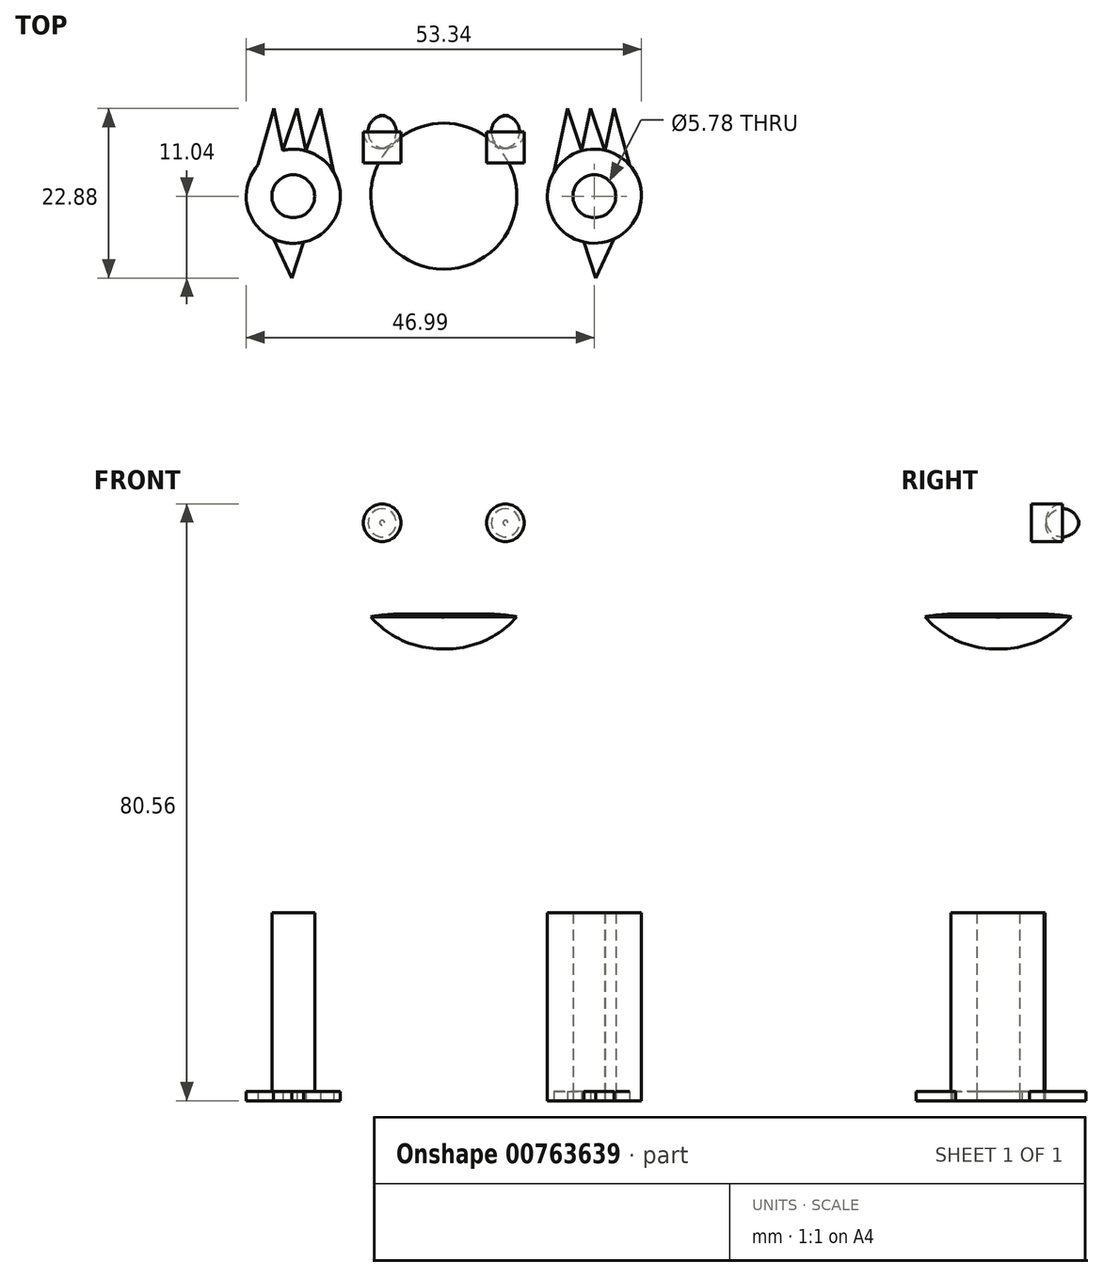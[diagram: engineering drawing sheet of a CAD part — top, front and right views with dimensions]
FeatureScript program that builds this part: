
annotation { "Feature Type Name" : "Feature", "Feature Type Description" : "" }
export const myFeature = defineFeature(function(context is Context, id is Id, definition is map)
    precondition{}
    {
        {
            var Q0;
            Q0=qCreatedBy(makeId("Top.planeOp"),FACE);
            var sketch = newSketch(context, id + "F0", { "sketchPlane" : qUnion([Q0])});
            skCircle(sketch, "E0", {"center": v(-20.32, 0) * mm, "radius": 6.35 * mm});
            skLineSegment(sketch, "E1", {"start": v(-23, -5.75) * mm, "end": v(-20.49, -11.04) * mm});
            skLineSegment(sketch, "E2", {"start": v(-18.95, -6.2) * mm, "end": v(-20.49, -11.04) * mm});
            skLineSegment(sketch, "E3.MirrorCS", {"start": v(18.95, -6.2) * mm, "end": v(20.49, -11.04) * mm});
            skLineSegment(sketch, "E4.MirrorCS", {"start": v(23, -5.75) * mm, "end": v(20.49, -11.04) * mm});
            skCircle(sketch, "E5.MirrorC", {"center": v(20.32, 0) * mm, "radius": 2.9 * mm});
            skCircle(sketch, "E6.MirrorC", {"center": v(20.32, 0) * mm, "radius": 6.35 * mm});
            skLineSegment(sketch, "E7", {"start": v(14.86, 3.24) * mm, "end": v(16.67, 11.84) * mm});
            skLineSegment(sketch, "E8", {"start": v(16.67, 11.84) * mm, "end": v(18.6, 6.12) * mm});
            skLineSegment(sketch, "E9", {"start": v(18.6, 6.12) * mm, "end": v(19.81, 11.84) * mm});
            skLineSegment(sketch, "E10", {"start": v(19.81, 11.84) * mm, "end": v(21.75, 6.12) * mm});
            skLineSegment(sketch, "E11", {"start": v(21.75, 6.12) * mm, "end": v(22.96, 11.84) * mm});
            skLineSegment(sketch, "E12", {"start": v(22.96, 11.84) * mm, "end": v(25.07, 4.22) * mm});
            skLineSegment(sketch, "E13.MirrorCS", {"start": v(-18.6, 6.12) * mm, "end": v(-19.81, 11.84) * mm});
            skCircle(sketch, "E14.MirrorC", {"center": v(-20.32, 0) * mm, "radius": 2.9 * mm});
            skLineSegment(sketch, "E15.MirrorCS", {"start": v(-16.67, 11.84) * mm, "end": v(-18.6, 6.12) * mm});
            skLineSegment(sketch, "E16.MirrorCS", {"start": v(-14.86, 3.24) * mm, "end": v(-16.67, 11.84) * mm});
            skLineSegment(sketch, "E17.MirrorCS", {"start": v(-22.96, 11.84) * mm, "end": v(-25.07, 4.22) * mm});
            skLineSegment(sketch, "E18.MirrorCS", {"start": v(-19.81, 11.84) * mm, "end": v(-21.75, 6.12) * mm});
            skLineSegment(sketch, "E19.MirrorCS", {"start": v(-21.75, 6.12) * mm, "end": v(-22.96, 11.84) * mm});
            skSolve(sketch);
        }
        {
            var Q0;
            Q0=makeQuery(id+"F0.imprint","IMPRINT",FACE,{"disambiguationData":[TD([[makeQuery(id+"F0.imprint","IMPRINT",EDGE,{"derivedFrom":sQuery(id+"F0.wireOp",EDGE,"E14.MirrorC")}),1.0]])]});
            var Q1;
            Q1=makeQuery(id+"F0.imprint","IMPRINT",FACE,{"disambiguationData":[TD([[makeQuery(id+"F0.imprint","IMPRINT",EDGE,{"derivedFrom":sQuery(id+"F0.wireOp",EDGE,"E5.MirrorC")}),-1.0]])]});
            extrude(context, id + "F1", {"entities" : qUnion([Q0, Q1]), "depth" : 25.4 * mm, "offsetDistance" : 25.4 * mm});
        }
        {
            var Q0;
            Q0=qCreatedBy(makeId("Front.planeOp"),FACE);
            var sketch = newSketch(context, id + "F2", { "sketchPlane" : qUnion([Q0])});
            skArc(sketch, "E20", {"start": v(0, 65.16) * mm, "mid": v(-32.14, 38.92) * mm, "end": v(0, 12.69) * mm});
            skLineSegment(sketch, "E21", {"start": v(0, 65.16) * mm, "end": v(0, 12.69) * mm});
            skSolve(sketch);
        }
        {
            var Q0;
            Q0=makeQuery(id+"F2.imprint","IMPRINT",FACE,{"disambiguationData":[TD([[makeQuery(id+"F2.imprint","IMPRINT",EDGE,{"derivedFrom":sQuery(id+"F2.wireOp",EDGE,"E20")}),1.0]])]});
            var Q1;
            Q1=sQuery(id+"F2.wireOp",EDGE,"E21");
            revolve(context, id + "F3", {"surfaceOperationType" : NewSurfaceOperationType.NEW, "entities" : qUnion([Q0]), "axis" : qUnion([Q1]), "revolveType" : RevolveType.FULL});
        }
        {
            var Q0;
            Q0=makeQuery(id+"F0.imprint","IMPRINT",FACE,{"disambiguationData":[TD([[makeQuery(id+"F0.imprint","IMPRINT",EDGE,{"derivedFrom":sQuery(id+"F0.wireOp",EDGE,"E14.MirrorC")}),-1.0]])]});
            extrude(context, id + "F4", {"entities" : qUnion([Q0]), "operationType" : NewBodyOperationType.ADD, "depth" : 1.27 * mm, "offsetDistance" : 25.4 * mm});
        }
        {
            var Q0;
            {var subQ0=sQuery(id+"F0.wireOp",EDGE,"E17.MirrorCS");Q0=makeQuery(id+"F0.imprint","IMPRINT",FACE,{"disambiguationData":[TD([[makeQuery(id+"F0.imprint","IMPRINT",EDGE,{"derivedFrom":subQ0}),1.0]])]});}
            extrude(context, id + "F5", {"entities" : qUnion([Q0]), "operationType" : NewBodyOperationType.ADD, "depth" : 1.27 * mm, "offsetDistance" : 25.4 * mm});
        }
        {
            var Q0;
            {var subQ0=sQuery(id+"F0.wireOp",EDGE,"E13.MirrorCS");Q0=makeQuery(id+"F0.imprint","IMPRINT",FACE,{"disambiguationData":[TD([[makeQuery(id+"F0.imprint","IMPRINT",EDGE,{"derivedFrom":subQ0}),1.0]])]});}
            var Q1;
            {var subQ0=sQuery(id+"F0.wireOp",EDGE,"E15.MirrorCS");Q1=makeQuery(id+"F0.imprint","IMPRINT",FACE,{"disambiguationData":[TD([[makeQuery(id+"F0.imprint","IMPRINT",EDGE,{"derivedFrom":subQ0}),1.0]])]});}
            var Q2;
            {var subQ0=sQuery(id+"F0.wireOp",EDGE,"E2");Q2=makeQuery(id+"F0.imprint","IMPRINT",FACE,{"disambiguationData":[TD([[makeQuery(id+"F0.imprint","IMPRINT",EDGE,{"derivedFrom":subQ0}),-1.0]])]});}
            var Q3;
            {var subQ0=sQuery(id+"F0.wireOp",EDGE,"E3.MirrorCS");Q3=makeQuery(id+"F0.imprint","IMPRINT",FACE,{"disambiguationData":[TD([[makeQuery(id+"F0.imprint","IMPRINT",EDGE,{"derivedFrom":subQ0}),1.0]])]});}
            var Q4;
            {var subQ0=sQuery(id+"F0.wireOp",EDGE,"E7");Q4=makeQuery(id+"F0.imprint","IMPRINT",FACE,{"disambiguationData":[TD([[makeQuery(id+"F0.imprint","IMPRINT",EDGE,{"derivedFrom":subQ0}),-1.0]])]});}
            var Q5;
            {var subQ0=sQuery(id+"F0.wireOp",EDGE,"E9");Q5=makeQuery(id+"F0.imprint","IMPRINT",FACE,{"disambiguationData":[TD([[makeQuery(id+"F0.imprint","IMPRINT",EDGE,{"derivedFrom":subQ0}),-1.0]])]});}
            var Q6;
            Q6=makeQuery(id+"F0.imprint","IMPRINT",FACE,{"disambiguationData":[TD([[makeQuery(id+"F0.imprint","IMPRINT",EDGE,{"derivedFrom":sQuery(id+"F0.wireOp",EDGE,"E5.MirrorC")}),1.0]])]});
            var Q7;
            {var subQ0=sQuery(id+"F0.wireOp",EDGE,"E12");Q7=makeQuery(id+"F0.imprint","IMPRINT",FACE,{"disambiguationData":[TD([[makeQuery(id+"F0.imprint","IMPRINT",EDGE,{"derivedFrom":subQ0}),-1.0]])]});}
            extrude(context, id + "F6", {"entities" : qUnion([Q0, Q1, Q2, Q3, Q4, Q5, Q6, Q7]), "depth" : 1.27 * mm, "offsetDistance" : 25.4 * mm});
        }
        {
            var Q0;
            Q0=qCreatedBy(makeId("Front.planeOp"),FACE);
            var sketch = newSketch(context, id + "F7", { "sketchPlane" : qUnion([Q0])});
            skLineSegment(sketch, "E22", {"start": v(0, 61) * mm, "end": v(0, 86.4) * mm});
            skArc(sketch, "E23", {"start": v(0, 86.4) * mm, "mid": v(-13, 73.7) * mm, "end": v(0, 61) * mm});
            skSolve(sketch);
        }
        {
            var Q0;
            Q0=makeQuery(id+"F7.imprint","IMPRINT",FACE,{"disambiguationData":[TD([[makeQuery(id+"F7.imprint","IMPRINT",EDGE,{"derivedFrom":sQuery(id+"F7.wireOp",EDGE,"E22")}),1.0]])]});
            var Q1;
            Q1=sQuery(id+"F7.wireOp",EDGE,"E22");
            revolve(context, id + "F8", {"operationType" : NewBodyOperationType.ADD, "surfaceOperationType" : NewSurfaceOperationType.NEW, "entities" : qUnion([Q0]), "axis" : qUnion([Q1]), "revolveType" : RevolveType.FULL});
        }
        {
            var Q0;
            Q0=qCreatedBy(makeId("Front.planeOp"),FACE);
            var sketch = newSketch(context, id + "F9", { "sketchPlane" : qUnion([Q0])});
            skCircle(sketch, "E24", {"center": v(0, 75.92) * mm, "radius": 1.47 * mm});
            skSolve(sketch);
        }
        {
            var Q0;
            Q0=sQuery(id+"F9.wireOp",EDGE,"E24");
            extrude(context, id + "F10", {"bodyType" : ToolBodyType.SURFACE, "surfaceEntities" : qUnion([Q0]), "oppositeDirection" : true, "depth" : 13.46 * mm, "offsetDistance" : 25.4 * mm});
        }
        {
            var Q0;
            Q0=qCreatedBy(makeId("Right.planeOp"),FACE);
            var sketch = newSketch(context, id + "F11", { "sketchPlane" : qUnion([Q0])});
            skPoint(sketch, "E25", {"position": v(17.1, 75.94) * mm});
            skSolve(sketch);
        }
        {
            var Q0;
            Q0=makeQuery(id+"F10.opExtrude","SWEPT_BODY",BODY,{"disambiguationData":[OSD([sQuery(id+"F9.wireOp",EDGE,"E24")])]});
            var Q1;
            Q1=makeQuery(id+"F10.opExtrude","CAP_EDGE",EDGE,{"disambiguationData":[OSD([sQuery(id+"F9.wireOp",EDGE,"E24")])],"isStart":false});
            var Q2;
            Q2=sQuery(id+"F11.wireOp",VERTEX,"E25");
            loft(context, id + "F12", {"bodyType" : ToolBodyType.SURFACE, "surfaceOperationType" : NewSurfaceOperationType.ADD, "sheetProfilesArray" : [{ "sheetProfileEntities" : qUnion([Q0]) }], "wireProfilesArray" : [{ "wireProfileEntities" : qUnion([Q1]) }, { "wireProfileEntities" : qUnion([Q2]) }]});
        }
        {
            var Q0;
            Q0=qCreatedBy(makeId("Front.planeOp"),FACE);
            cPlane(context, id + "F13", {"entities" : qUnion([Q0]), "cplaneType" : CPlaneType.OFFSET, "offset" : 10.16 * mm, "oppositeDirection" : true, "width" : 152.4 * mm, "height" : 152.4 * mm});
        }
        {
            var Q0;
            Q0=qCreatedBy(id+"F13.planeOp",FACE);
            var sketch = newSketch(context, id + "F14", { "sketchPlane" : qUnion([Q0])});
            skCircle(sketch, "E26", {"center": v(8.32, 78.02) * mm, "radius": 2.54 * mm});
            skCircle(sketch, "E27", {"center": v(-8.32, 78.02) * mm, "radius": 2.54 * mm});
            skSolve(sketch);
        }
        {
            var Q0;
            Q0 = qSketchRegion(id + "F14", true);
            extrude(context, id + "F15", {"entities" : qUnion([Q0]), "oppositeDirection" : true, "depth" : 0.76 * mm, "offsetDistance" : 25.4 * mm, "hasSecondDirection" : true, "secondDirectionOppositeDirection" : false, "secondDirectionDepth" : 5.66 * mm});
        }
        {
            var Q0;
            Q0=makeQuery(id+"F15.opExtrude","CAP_FACE",FACE,{"disambiguationData":[OSD([sQuery(id+"F14.wireOp",EDGE,"E27")])],"isStart":false});
            var Q1;
            Q1=makeQuery(id+"F15.opExtrude","CAP_FACE",FACE,{"disambiguationData":[OSD([sQuery(id+"F14.wireOp",EDGE,"E26")])],"isStart":false});
            fillet(context, id + "F16", {"entities" : qUnion([Q0, Q1]), "radius" : 2.22 * mm, "tangentPropagation" : true, "allowEdgeOverflow" : false});
        }
        {
            var Q0;
            Q0=qCreatedBy(makeId("Right.planeOp"),FACE);
            cPlane(context, id + "F17", {"entities" : qUnion([Q0]), "cplaneType" : CPlaneType.OFFSET, "offset" : 30.48 * mm, "width" : 152.4 * mm, "height" : 152.4 * mm});
        }
        {
            var Q0;
            Q0=qCreatedBy(id+"F17.planeOp",FACE);
            var sketch = newSketch(context, id + "F18", { "sketchPlane" : qUnion([Q0])});
            skLineSegment(sketch, "E28", {"start": v(-10.4, 41.11) * mm, "end": v(11.18, 41.11) * mm});
            skArc(sketch, "E29", {"start": v(-10.4, 41.11) * mm, "mid": v(0.39, 30.32) * mm, "end": v(11.18, 41.11) * mm});
            skSolve(sketch);
        }
        {
            var Q0;
            Q0=sQuery(id+"F18.wireOp",EDGE,"E29");
            var Q1;
            Q1=sQuery(id+"F18.wireOp",EDGE,"E28");
            revolve(context, id + "F19", {"bodyType" : ToolBodyType.SURFACE, "surfaceOperationType" : NewSurfaceOperationType.NEW, "surfaceEntities" : qUnion([Q0]), "axis" : qUnion([Q1]), "revolveType" : RevolveType.FULL});
        }
        {
            var Q0;
            Q0=qCreatedBy(makeId("Right.planeOp"),FACE);
            cPlane(context, id + "F20", {"entities" : qUnion([Q0]), "cplaneType" : CPlaneType.OFFSET, "offset" : 30.48 * mm, "oppositeDirection" : true, "width" : 152.4 * mm, "height" : 152.4 * mm});
        }
        {
            var Q0;
            Q0=qCreatedBy(id+"F20.planeOp",FACE);
            var sketch = newSketch(context, id + "F21", { "sketchPlane" : qUnion([Q0])});
            skLineSegment(sketch, "E30", {"start": v(11.65, 39.34) * mm, "end": v(-9.93, 39.34) * mm});
            skArc(sketch, "E31", {"start": v(-9.93, 39.34) * mm, "mid": v(0.86, 28.55) * mm, "end": v(11.65, 39.34) * mm});
            skSolve(sketch);
        }
        {
            var Q0;
            Q0=sQuery(id+"F21.wireOp",EDGE,"E31");
            var Q1;
            Q1=sQuery(id+"F21.wireOp",EDGE,"E30");
            revolve(context, id + "F22", {"bodyType" : ToolBodyType.SURFACE, "surfaceOperationType" : NewSurfaceOperationType.NEW, "surfaceEntities" : qUnion([Q0]), "axis" : qUnion([Q1]), "revolveType" : RevolveType.FULL});
        }
    });
